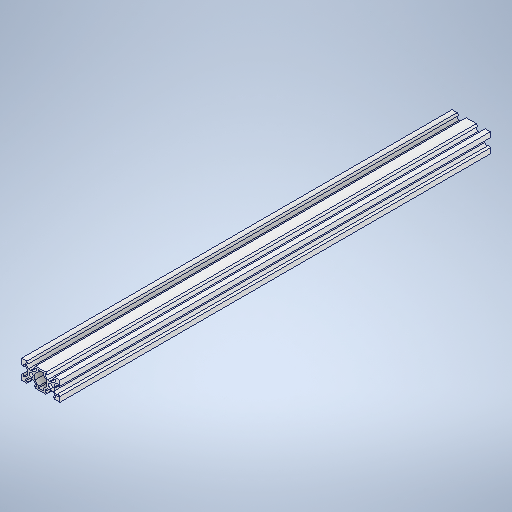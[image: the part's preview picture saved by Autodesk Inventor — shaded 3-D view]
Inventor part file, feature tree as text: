
AUTODESK INVENTOR PART (.ipt)
format: ipt  version: 2025.2 (Build 292293000, 293)  size: 384,512 bytes
history: native  units: in
note: dims shown in document units (in); Inventor stores cm internally (conversion verified against a paired STEP export)
features: extrude x1, sketch x1, other x1
ambient origin geometry x8: Origin, YZ Plane, XZ Plane, XY Plane, X Axis, Y Axis, Z Axis, Center Point
bodies: Solid1 (feature_tree)
feature tree (3):
  extrude  "Extrusion1"  [1 undecoded]
  sketch  "Sketch1"  dims[d0=1.9685in d1=0.0in]
  other  "Boss-Extrude1"
note: 1 required parameter value undecoded (feature->parameter linkage not recoverable at this tier; creation-order binding heuristic only, values carry confidence <= 0.55)
